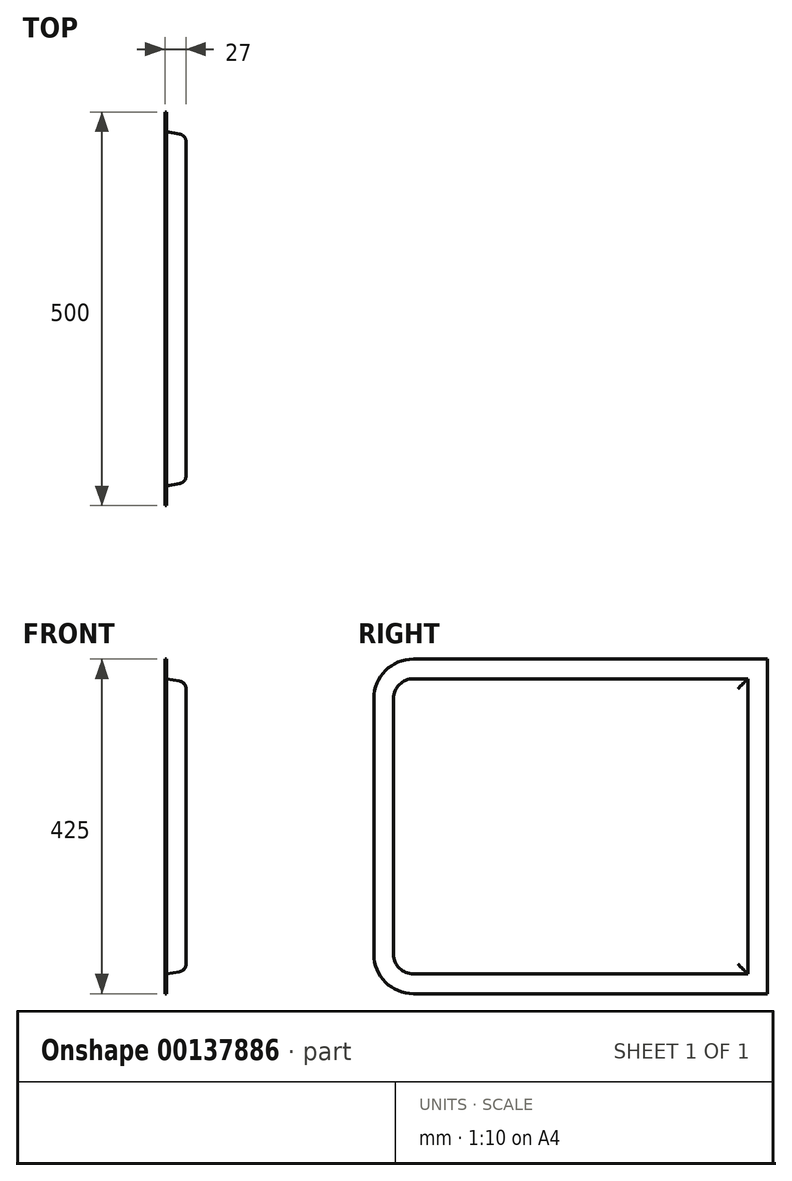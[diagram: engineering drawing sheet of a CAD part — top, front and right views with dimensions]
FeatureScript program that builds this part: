
annotation { "Feature Type Name" : "Feature", "Feature Type Description" : "" }
export const myFeature = defineFeature(function(context is Context, id is Id, definition is map)
    precondition{}
    {
        {
            var Q0;
            Q0=qCreatedBy(makeId("Right.planeOp"),FACE);
            var sketch = newSketch(context, id + "F0", { "sketchPlane" : qUnion([Q0])});
            skLineSegment(sketch, "E0.bottom", {"start": v(250, -212.5) * mm, "end": v(-200, -212.5) * mm});
            skLineSegment(sketch, "E0.top", {"start": v(250, 212.5) * mm, "end": v(-200, 212.5) * mm});
            skLineSegment(sketch, "E0.left", {"start": v(250, -212.5) * mm, "end": v(250, 212.5) * mm});
            skLineSegment(sketch, "E0.right", {"start": v(-250, -162.5) * mm, "end": v(-250, 162.5) * mm});
            skPoint(sketch, "E0.middle", {"position": v(0, 0) * mm});
            skPoint(sketch, "E1.visualSharp", {"position": v(-250, 212.5) * mm});
            skArc(sketch, "E1.filletArc", {"start": v(-200, 212.5) * mm, "mid": v(-235.36, 197.86) * mm, "end": v(-250, 162.5) * mm});
            skPoint(sketch, "E2.visualSharp", {"position": v(-250, -212.5) * mm});
            skArc(sketch, "E2.filletArc", {"start": v(-250, -162.5) * mm, "mid": v(-235.36, -197.86) * mm, "end": v(-200, -212.5) * mm});
            skLineSegment(sketch, "E3.0", {"start": v(225, -187.5) * mm, "end": v(225, 187.5) * mm});
            skArc(sketch, "E3.1", {"start": v(-225, -162.5) * mm, "mid": v(-217.68, -180.18) * mm, "end": v(-200, -187.5) * mm});
            skLineSegment(sketch, "E3.2", {"start": v(-225, -162.5) * mm, "end": v(-225, 162.5) * mm});
            skLineSegment(sketch, "E3.3", {"start": v(225, -187.5) * mm, "end": v(-200, -187.5) * mm});
            skArc(sketch, "E3.4", {"start": v(-200, 187.5) * mm, "mid": v(-217.68, 180.18) * mm, "end": v(-225, 162.5) * mm});
            skLineSegment(sketch, "E3.5", {"start": v(225, 187.5) * mm, "end": v(-200, 187.5) * mm});
            skSolve(sketch);
        }
        {
            var Q0;
            Q0=makeQuery(id+"F0.imprint","IMPRINT",FACE,{"disambiguationData":[TD([[makeQuery(id+"F0.imprint","IMPRINT",EDGE,{"derivedFrom":sQuery(id+"F0.wireOp",EDGE,"E3.0")}),1.0]])]});
            extrude(context, id + "F1", {"entities" : qUnion([Q0]), "depth" : 25 * mm, "hasDraft" : true, "draftAngle" : 10 * degree, "draftPullDirection" : true});
        }
        {
            var Q0;
            Q0=makeQuery(id+"F0.imprint","IMPRINT",FACE,{"disambiguationData":[TD([[makeQuery(id+"F0.imprint","IMPRINT",EDGE,{"derivedFrom":sQuery(id+"F0.wireOp",EDGE,"E0.bottom")}),-1.0]])]});
            var Q1;
            Q1=makeQuery(id+"F0.imprint","IMPRINT",FACE,{"disambiguationData":[TD([[makeQuery(id+"F0.imprint","IMPRINT",EDGE,{"derivedFrom":sQuery(id+"F0.wireOp",EDGE,"E3.0")}),1.0]])]});
            extrude(context, id + "F2", {"entities" : qUnion([Q0, Q1]), "operationType" : NewBodyOperationType.ADD, "oppositeDirection" : true, "depth" : 2 * mm});
        }
        {
            var Q0;
            Q0=makeQuery(id+"F1.opExtrude","CAP_EDGE",EDGE,{"disambiguationData":[OSD([sQuery(id+"F0.wireOp",EDGE,"E3.0")])],"isStart":false});
            var Q1;
            Q1=makeQuery(id+"F1.opExtrude","CAP_EDGE",EDGE,{"disambiguationData":[OSD([sQuery(id+"F0.wireOp",EDGE,"E3.3")])],"isStart":false});
            var Q2;
            Q2=makeQuery(id+"F1.opExtrude","CAP_EDGE",EDGE,{"disambiguationData":[OSD([sQuery(id+"F0.wireOp",EDGE,"E3.2")])],"isStart":false});
            var Q3;
            Q3=makeQuery(id+"F1.opExtrude","CAP_EDGE",EDGE,{"disambiguationData":[OSD([sQuery(id+"F0.wireOp",EDGE,"E3.1")])],"isStart":false});
            var Q4;
            Q4=makeQuery(id+"F1.opExtrude","CAP_EDGE",EDGE,{"disambiguationData":[OSD([sQuery(id+"F0.wireOp",EDGE,"E3.5")])],"isStart":false});
            var Q5;
            Q5=makeQuery(id+"F1.opExtrude","CAP_EDGE",EDGE,{"disambiguationData":[OSD([sQuery(id+"F0.wireOp",EDGE,"E3.4")])],"isStart":false});
            var Q6;
            Q6=makeQuery(id+"F1.opExtrude","CAP_EDGE",EDGE,{"disambiguationData":[OSD([sQuery(id+"F0.wireOp",EDGE,"E3.3")])],"isStart":true});
            fillet(context, id + "F3", {"entities" : qUnion([Q0, Q1, Q2, Q3, Q4, Q5, Q6]), "radius" : 10 * mm, "tangentPropagation" : true, "allowEdgeOverflow" : false});
        }
    });
